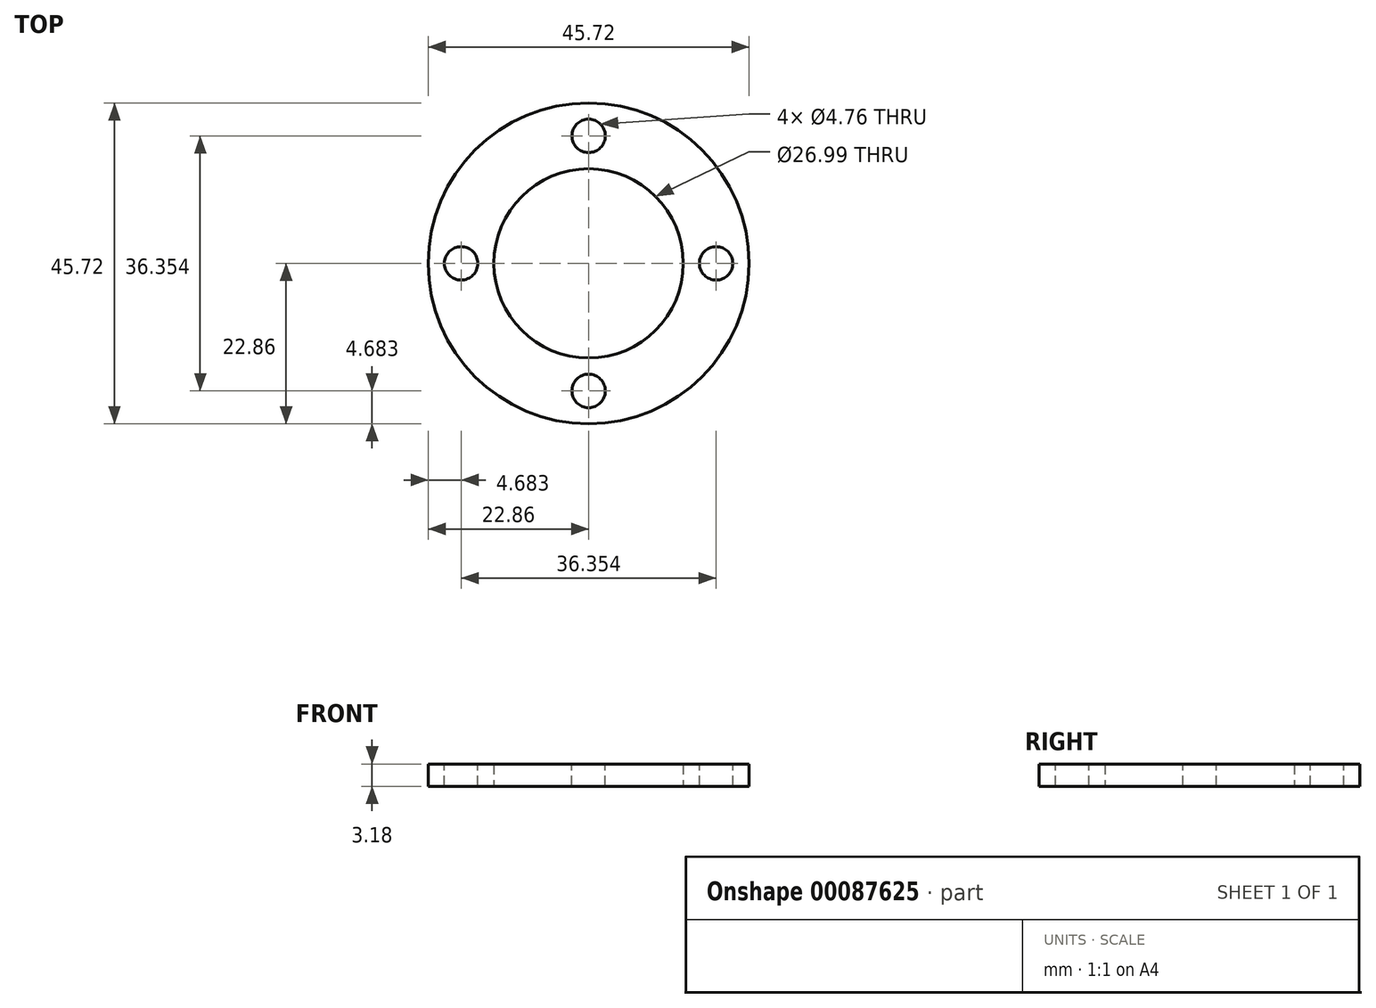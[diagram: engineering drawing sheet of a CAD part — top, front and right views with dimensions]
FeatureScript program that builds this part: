
annotation { "Feature Type Name" : "Feature", "Feature Type Description" : "" }
export const myFeature = defineFeature(function(context is Context, id is Id, definition is map)
    precondition{}
    {
        {
            var Q0;
            Q0=qCreatedBy(makeId("Top.planeOp"),FACE);
            var sketch = newSketch(context, id + "F0", { "sketchPlane" : qUnion([Q0])});
            skCircle(sketch, "E0", {"center": v(0, 0) * mm, "radius": 22.86 * mm});
            skCircle(sketch, "E1", {"center": v(0, 0) * mm, "radius": 13.5 * mm});
            skSolve(sketch);
        }
        {
            var Q0;
            Q0=makeQuery(id+"F0.imprint","IMPRINT",FACE,{"disambiguationData":[TD([[makeQuery(id+"F0.imprint","IMPRINT",EDGE,{"derivedFrom":sQuery(id+"F0.wireOp",EDGE,"E0")}),1.0]])]});
            extrude(context, id + "F1", {"entities" : qUnion([Q0]), "depth" : 3.17 * mm});
        }
        {
            var Q0;
            Q0=makeQuery(id+"F1.opExtrude","CAP_FACE",FACE,{"disambiguationData":[OSD([sQuery(id+"F0.wireOp",EDGE,"E0"),sQuery(id+"F0.wireOp",EDGE,"E1")])],"isStart":false});
            var sketch = newSketch(context, id + "F2", { "sketchPlane" : qUnion([Q0])});
            skLineSegment(sketch, "E2", {"start": v(0, 22.86) * mm, "end": v(0, 13.5) * mm});
            skCircle(sketch, "E3", {"center": v(0, 18.18) * mm, "radius": 2.38 * mm});
            skCircle(sketch, "E4.1.0", {"center": v(-18.18, 0) * mm, "radius": 2.38 * mm});
            skCircle(sketch, "E4.2.0", {"center": v(0, -18.18) * mm, "radius": 2.38 * mm});
            skCircle(sketch, "E4.3.0", {"center": v(18.18, 0) * mm, "radius": 2.38 * mm});
            skPoint(sketch, "E4.center", {"position": v(0, 0) * mm});
            skSolve(sketch);
        }
        {
            var Q0;
            {var subQ0=sQuery(id+"F2.wireOp",EDGE,"E3");var subQ1=sQuery(id+"F2.wireOp",EDGE,"E2");var subQ2=makeQuery(id+"F2.imprint","INTERSECT",VERTEX,{"disambiguationData":[OD(0.0)],"derivedFrom":[subQ1,subQ0]});Q0=makeQuery(id+"F2.imprint","IMPRINT",FACE,{"disambiguationData":[TD([[makeQuery(id+"F2.imprint","IMPRINT",EDGE,{"disambiguationData":[TD([[subQ2,1.0]])],"derivedFrom":subQ1}),1.0]])]});}
            var Q1;
            {var subQ0=sQuery(id+"F2.wireOp",EDGE,"E3");var subQ1=sQuery(id+"F2.wireOp",EDGE,"E2");var subQ2=makeQuery(id+"F2.imprint","INTERSECT",VERTEX,{"disambiguationData":[OD(0.0)],"derivedFrom":[subQ1,subQ0]});Q1=makeQuery(id+"F2.imprint","IMPRINT",FACE,{"disambiguationData":[TD([[makeQuery(id+"F2.imprint","IMPRINT",EDGE,{"disambiguationData":[TD([[subQ2,1.0]])],"derivedFrom":subQ1}),-1.0]])]});}
            var Q2;
            Q2=makeQuery(id+"F2.imprint","IMPRINT",FACE,{"disambiguationData":[TD([[makeQuery(id+"F2.imprint","IMPRINT",EDGE,{"derivedFrom":sQuery(id+"F2.wireOp",EDGE,"E4.1.0")}),1.0]])]});
            var Q3;
            Q3=makeQuery(id+"F2.imprint","IMPRINT",FACE,{"disambiguationData":[TD([[makeQuery(id+"F2.imprint","IMPRINT",EDGE,{"derivedFrom":sQuery(id+"F2.wireOp",EDGE,"E4.2.0")}),1.0]])]});
            var Q4;
            Q4=makeQuery(id+"F2.imprint","IMPRINT",FACE,{"disambiguationData":[TD([[makeQuery(id+"F2.imprint","IMPRINT",EDGE,{"derivedFrom":sQuery(id+"F2.wireOp",EDGE,"E4.3.0")}),1.0]])]});
            extrude(context, id + "F3", {"entities" : qUnion([Q0, Q1, Q2, Q3, Q4]), "operationType" : NewBodyOperationType.REMOVE, "oppositeDirection" : true, "depth" : 25.4 * mm});
        }
    });
